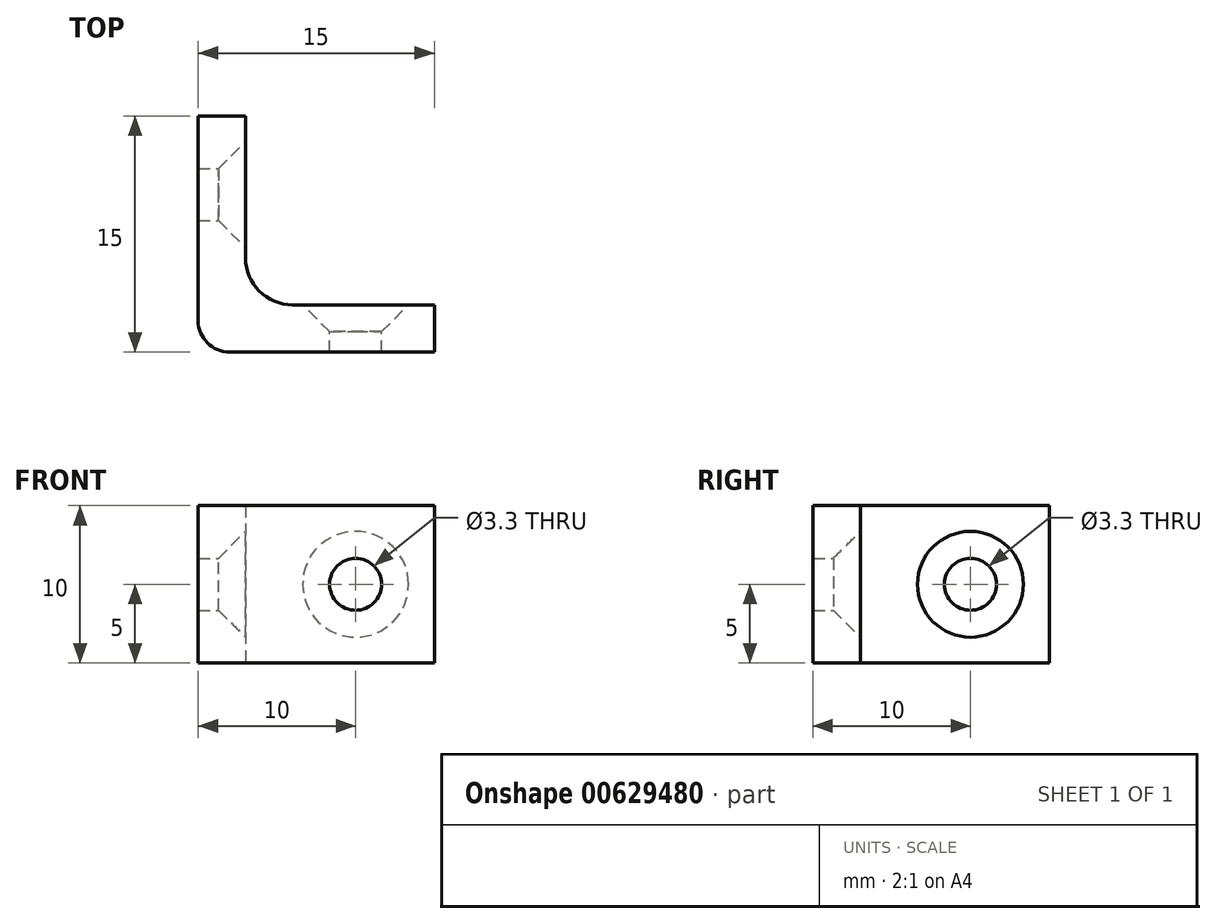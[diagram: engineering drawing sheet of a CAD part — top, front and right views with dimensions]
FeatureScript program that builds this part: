
annotation { "Feature Type Name" : "Feature", "Feature Type Description" : "" }
export const myFeature = defineFeature(function(context is Context, id is Id, definition is map)
    precondition{}
    {
        {
            var Q0;
            Q0=qCreatedBy(makeId("Top.planeOp"),FACE);
            var sketch = newSketch(context, id + "F0", { "sketchPlane" : qUnion([Q0])});
            skLineSegment(sketch, "E0", {"start": v(0, 0) * mm, "end": v(0, 15) * mm});
            skLineSegment(sketch, "E1", {"start": v(0, 15) * mm, "end": v(3, 15) * mm});
            skLineSegment(sketch, "E2", {"start": v(3, 15) * mm, "end": v(3, 6) * mm});
            skLineSegment(sketch, "E3", {"start": v(6, 3) * mm, "end": v(15, 3) * mm});
            skLineSegment(sketch, "E4", {"start": v(15, 3) * mm, "end": v(15, 0) * mm});
            skLineSegment(sketch, "E5", {"start": v(15, 0) * mm, "end": v(0, 0) * mm});
            skPoint(sketch, "E6.visualSharp", {"position": v(3, 3) * mm});
            skArc(sketch, "E6.filletArc", {"start": v(3, 6) * mm, "mid": v(3.88, 3.88) * mm, "end": v(6, 3) * mm});
            skSolve(sketch);
        }
        {
            var Q0;
            Q0=makeQuery(id+"F0.imprint","IMPRINT",FACE,{"disambiguationData":[TD([[makeQuery(id+"F0.imprint","IMPRINT",EDGE,{"derivedFrom":sQuery(id+"F0.wireOp",EDGE,"E0")}),-1.0]])]});
            extrude(context, id + "F1", {"entities" : qUnion([Q0]), "depth" : 10 * mm, "offsetDistance" : 25 * mm});
        }
        {
            var Q0;
            Q0=makeQuery(id+"F1.opExtrude","SWEPT_FACE",FACE,{"disambiguationData":[OSD([sQuery(id+"F0.wireOp",EDGE,"E2")])]});
            var sketch = newSketch(context, id + "F2", { "sketchPlane" : qUnion([Q0])});
            skPoint(sketch, "E7", {"position": v(10, 5) * mm});
            skPoint(sketch, "E7.positionSnap0", {"position": v(15, 5) * mm});
            skSolve(sketch);
        }
        {
            var Q0;
            Q0=sQuery(id+"F2.wireOp",VERTEX,"E7");
            var Q1;
            Q1=makeQuery(id+"F1.opExtrude","SWEPT_BODY",BODY,{"disambiguationData":[OSD([sQuery(id+"F0.wireOp",EDGE,"E0"),sQuery(id+"F0.wireOp",EDGE,"E1"),sQuery(id+"F0.wireOp",EDGE,"E2"),sQuery(id+"F0.wireOp",EDGE,"E3"),sQuery(id+"F0.wireOp",EDGE,"E4"),sQuery(id+"F0.wireOp",EDGE,"E5"),sQuery(id+"F0.wireOp",EDGE,"E6.filletArc")])]});
            hole(context, id + "F3", {"style" : HoleStyle.C_SINK, "endStyle" : HoleEndStyle.THROUGH, "standardTappedOrClearance" : lookupTablePath({ "standard" : "ISO", "fit" : "Normal", "size" : "M3", "type" : "Clearance" }), "standardBlindInLast" : lookupTablePath({ "fit" : "Standard", "standard" : "ISO", "size" : "M3", "type" : "Clearance" }), "holeDiameter" : 3.3 * mm, "cSinkDiameter" : 6.72 * mm, "cSinkAngle" : 90 * degree, "majorDiameter" : 3 * mm, "isTappedThrough" : true, "tappedDepth" : 12 * mm, "tapClearance" : 3, "locations" : qUnion([Q0]), "scope" : qUnion([Q1])});
        }
        {
            var Q0;
            Q0=makeQuery(id+"F1.opExtrude","SWEPT_FACE",FACE,{"disambiguationData":[OSD([sQuery(id+"F0.wireOp",EDGE,"E3")])]});
            var sketch = newSketch(context, id + "F4", { "sketchPlane" : qUnion([Q0])});
            skPoint(sketch, "E8", {"position": v(-10, 5) * mm});
            skPoint(sketch, "E8.positionSnap0", {"position": v(-15, 5) * mm});
            skPoint(sketch, "E8.positionSnap1", {"position": v(-10, 0) * mm});
            skSolve(sketch);
        }
        {
            var Q0;
            Q0=sQuery(id+"F4.wireOp",VERTEX,"E8");
            var Q1;
            Q1=makeQuery(id+"F1.opExtrude","SWEPT_BODY",BODY,{"disambiguationData":[OSD([sQuery(id+"F0.wireOp",EDGE,"E0"),sQuery(id+"F0.wireOp",EDGE,"E1"),sQuery(id+"F0.wireOp",EDGE,"E2"),sQuery(id+"F0.wireOp",EDGE,"E3"),sQuery(id+"F0.wireOp",EDGE,"E4"),sQuery(id+"F0.wireOp",EDGE,"E5"),sQuery(id+"F0.wireOp",EDGE,"E6.filletArc")])]});
            hole(context, id + "F5", {"style" : HoleStyle.C_SINK, "endStyle" : HoleEndStyle.THROUGH, "standardTappedOrClearance" : lookupTablePath({ "standard" : "ISO", "fit" : "Normal", "size" : "M3", "type" : "Clearance" }), "standardBlindInLast" : lookupTablePath({ "fit" : "Standard", "standard" : "ISO", "size" : "M3", "type" : "Clearance" }), "holeDiameter" : 3.3 * mm, "cSinkDiameter" : 6.72 * mm, "cSinkAngle" : 90 * degree, "majorDiameter" : 5 * mm, "isTappedThrough" : true, "tappedDepth" : 12 * mm, "tapClearance" : 3, "locations" : qUnion([Q0]), "scope" : qUnion([Q1])});
        }
        {
            var Q0;
            Q0=makeQuery(id+"F1.opExtrude","SWEPT_EDGE",EDGE,{"disambiguationData":[OSD([sQuery(id+"F0.wireOp",EDGE,"E0"),sQuery(id+"F0.wireOp",EDGE,"E5")])]});
            fillet(context, id + "F6", {"entities" : qUnion([Q0]), "radius" : 2 * mm, "tangentPropagation" : true, "allowEdgeOverflow" : false});
        }
    });
